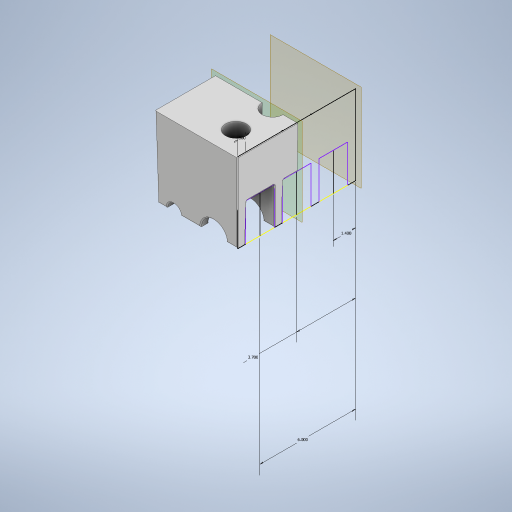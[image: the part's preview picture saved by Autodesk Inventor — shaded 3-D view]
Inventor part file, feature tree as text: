
AUTODESK INVENTOR PART (.ipt)
format: ipt  version: 2023 (Build 270158000, 158)  size: 754,688 bytes
history: native  units: in
note: dims shown in document units (in); Inventor stores cm internally (conversion verified against a paired STEP export)
features: draft x6, extrude x5, sketch x4, fillet x1, plane x1
ambient origin geometry x8: Origin, YZ Plane, XZ Plane, XY Plane, X Axis, Y Axis, Z Axis, Center Point
bodies: Solid1 (feature_tree)
feature tree (17):
  extrude  "Extrusion1"  Depth=5.0in
  sketch  "Sketch2"  dims[d3=7.4in d4=0.0in d6=1.4in]
  extrude  "Extrusion2"  Depth=1.4in
  extrude  "Extrusion3"  Depth=1.4in
  extrude  "Extrusion4"  Depth=0.0625in
  draft  "FaceDraft1"
  draft  "FaceDraft2"
  draft  "FaceDraft3"
  draft  "FaceDraft4"
  draft  "FaceDraft5"
  draft  "FaceDraft6"
  fillet  "Fillet1"  Radius=1.5in
  plane  "Work Plane1"
  extrude  "Extrusion5"  Depth=0.0625in
  sketch  "Sketch1"  dims[d0=5.0in d2=1.625in]
  sketch  "Sketch4"  dims[d7=1.5in d10=1.4in]
  sketch  "Sketch5"  dims[d11=1.5in d13=2.3in d14=1.5in d15=1.4in d16=3.7in d17=6.0in d18=0.5in d20=2.528in d21=7.4in d22=0.0in d23=7.4in d24=0.0in d25=1.5in d26=0.866in d27=1.5in d28=0.0in d29=1.4in d30=5.0in d31=-0.0069in d32=0.0069in d33=0.0069in d34=0.0069in d35=0.0069in d36=0.0069in d37=0.0625in d38=9.0in d39=0.0in]
